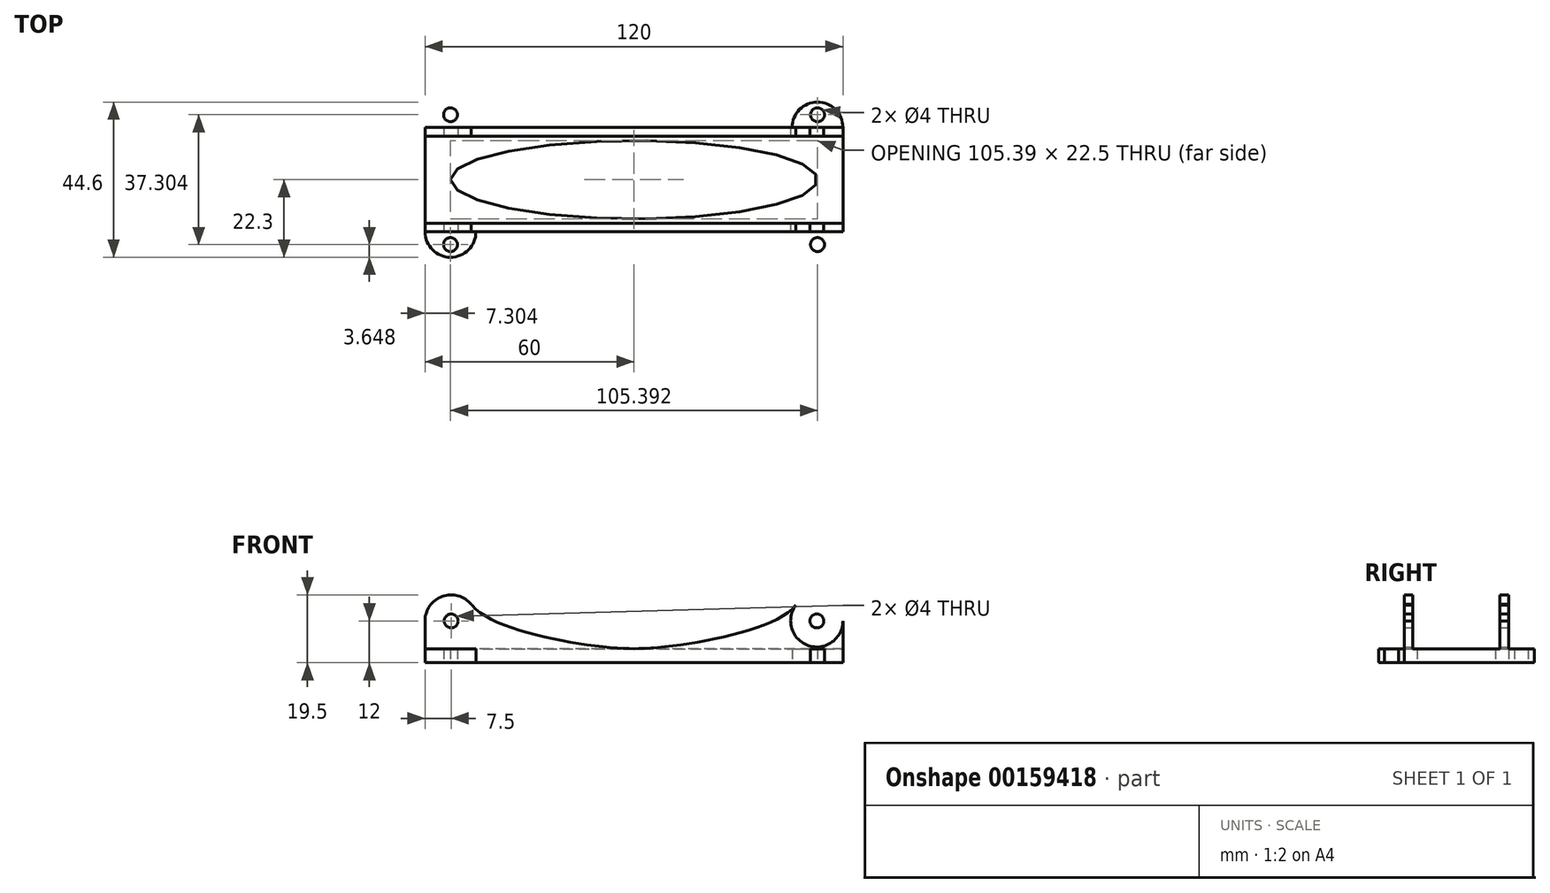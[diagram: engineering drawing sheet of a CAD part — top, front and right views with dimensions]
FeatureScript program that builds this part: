
annotation { "Feature Type Name" : "Feature", "Feature Type Description" : "" }
export const myFeature = defineFeature(function(context is Context, id is Id, definition is map)
    precondition{}
    {
        {
            assignVariable(context, id + "F0", {"mode" : VariableMode.ASSIGNED, "variableType" : VariableType.LENGTH, "measurementMode" : VariableMeasurementMode.DISTANCE, "name" : "channelWidth", "lengthValue" : 25 * mm, "minmax" : VariableMinMaxSelection.MINIMUM, "extendEntities" : false, "measureFromAxis" : false, "distance" : 0 * mm, "xOffset" : 0 * mm, "yOffset" : 0 * mm, "zOffset" : 0 * mm, "componentSelector" : AxisWithCustom.DISTANCE, "customOffset" : 0 * mm, "radius" : false, "description" : ""});
        }
        {
            var Q0;
            Q0=qCreatedBy(makeId("Front.planeOp"),FACE);
            var sketch = newSketch(context, id + "F1", { "sketchPlane" : qUnion([Q0])});
            skLineSegment(sketch, "E0", {"start": v(-52.5, 0) * mm, "end": v(52.5, 0) * mm, "construction": true});
            skPoint(sketch, "E1", {"position": v(-52.5, 0) * mm});
            skPoint(sketch, "E2", {"position": v(52.5, 0) * mm});
            skCircle(sketch, "E3", {"center": v(-52.5, 0) * mm, "radius": 7.5 * mm});
            skLineSegment(sketch, "E4", {"start": v(-60, 0) * mm, "end": v(-60, -12) * mm});
            skLineSegment(sketch, "E5", {"start": v(-60, -12) * mm, "end": v(0, -12) * mm});
            skLineSegment(sketch, "E6", {"start": v(0, -12) * mm, "end": v(0, -8) * mm});
            skFitSpline(sketch, "E7", {"points": [v(0, -8) * mm, v(-46.7, 4.76) * mm], "startDerivative": vector(-30.75, 0) * mm, "endDerivative": vector(-19.19, 25.66) * mm});
            skCircle(sketch, "E8", {"center": v(-52.5, 0) * mm, "radius": 2 * mm});
            skFitSpline(sketch, "E9.MirrorCS", {"points": [v(0, -8) * mm, v(46.7, 4.76) * mm], "startDerivative": vector(30.75, 0) * mm, "endDerivative": vector(19.19, 25.66) * mm});
            skLineSegment(sketch, "E10.MirrorCS", {"start": v(60, -12) * mm, "end": v(0, -12) * mm});
            skLineSegment(sketch, "E11.MirrorCS", {"start": v(60, 0) * mm, "end": v(60, -12) * mm});
            skCircle(sketch, "E12.MirrorC", {"center": v(52.5, 0) * mm, "radius": 7.5 * mm});
            skCircle(sketch, "E13.MirrorC", {"center": v(52.5, 0) * mm, "radius": 2 * mm});
            skLineSegment(sketch, "E14.bottom", {"start": v(0, -8) * mm, "end": v(-60, -8) * mm});
            skLineSegment(sketch, "E14.top", {"start": v(0, 11.94) * mm, "end": v(-60, 11.94) * mm});
            skLineSegment(sketch, "E14.left", {"start": v(0, -8) * mm, "end": v(0, 11.94) * mm});
            skLineSegment(sketch, "E14.right", {"start": v(-60, -8) * mm, "end": v(-60, 11.94) * mm});
            skLineSegment(sketch, "E15.MirrorCS", {"start": v(0, 11.94) * mm, "end": v(60, 11.94) * mm});
            skLineSegment(sketch, "E16.MirrorCS", {"start": v(60, -8) * mm, "end": v(60, 11.94) * mm});
            skLineSegment(sketch, "E17.MirrorCS", {"start": v(0, -8) * mm, "end": v(60, -8) * mm});
            skSolve(sketch);
        }
        {
            var Q0;
            {var subQ4=sQuery(id+"F1.wireOp",EDGE,"E4");Q0=makeQuery(id+"F1.imprint","IMPRINT",FACE,{"disambiguationData":[TD([[makeQuery(id+"F1.imprint","IMPRINT",EDGE,{"derivedFrom":subQ4}),1.0]])]});}
            var Q1;
            Q1=makeQuery(id+"F1.imprint","IMPRINT",FACE,{"disambiguationData":[TD([[makeQuery(id+"F1.imprint","IMPRINT",EDGE,{"derivedFrom":sQuery(id+"F1.wireOp",EDGE,"E8")}),-1.0]])]});
            var Q2;
            {var subQ1=sQuery(id+"F1.wireOp",EDGE,"E6");Q2=makeQuery(id+"F1.imprint","IMPRINT",FACE,{"disambiguationData":[TD([[makeQuery(id+"F1.imprint","IMPRINT",EDGE,{"derivedFrom":subQ1}),-1.0]])]});}
            var Q3;
            Q3=makeQuery(id+"F1.imprint","IMPRINT",FACE,{"disambiguationData":[TD([[makeQuery(id+"F1.imprint","IMPRINT",EDGE,{"derivedFrom":sQuery(id+"F1.wireOp",EDGE,"E13.MirrorC")}),1.0]])]});
            var Q4;
            {var subQ5=sQuery(id+"F1.wireOp",EDGE,"E14.bottom");Q4=makeQuery(id+"F1.imprint","IMPRINT",FACE,{"disambiguationData":[TD([[makeQuery(id+"F1.imprint","IMPRINT",EDGE,{"derivedFrom":subQ5}),-1.0]])]});}
            var Q5;
            {var subQ0=sQuery(id+"F1.wireOp",EDGE,"E17.MirrorCS");Q5=makeQuery(id+"F1.imprint","IMPRINT",FACE,{"disambiguationData":[TD([[makeQuery(id+"F1.imprint","IMPRINT",EDGE,{"derivedFrom":subQ0}),1.0]])]});}
            extrude(context, id + "F2", {"entities" : qUnion([Q0, Q1, Q2, Q3, Q4, Q5]), "flatOperationType" : FlatOperationType.REMOVE, "offsetDistance" : 25 * mm, "depth" : getVariable(context, 'channelWidth') + 5 * mm, "symmetric" : true, "domain" : OperationDomain.MODEL});
        }
        {
            var Q0;
            {var subQ4=sQuery(id+"F1.wireOp",EDGE,"E14.top");Q0=makeQuery(id+"F1.imprint","IMPRINT",FACE,{"disambiguationData":[TD([[makeQuery(id+"F1.imprint","IMPRINT",EDGE,{"derivedFrom":subQ4}),1.0]])]});}
            var Q1;
            {var subQ0=sQuery(id+"F1.wireOp",EDGE,"E14.left");Q1=makeQuery(id+"F1.imprint","IMPRINT",FACE,{"disambiguationData":[TD([[makeQuery(id+"F1.imprint","IMPRINT",EDGE,{"derivedFrom":subQ0}),-1.0]])]});}
            var Q2;
            Q2=makeQuery(id+"F1.imprint","IMPRINT",FACE,{"disambiguationData":[TD([[makeQuery(id+"F1.imprint","IMPRINT",EDGE,{"derivedFrom":sQuery(id+"F1.wireOp",EDGE,"E8")}),-1.0]])]});
            var Q3;
            Q3=makeQuery(id+"F1.imprint","IMPRINT",FACE,{"disambiguationData":[TD([[makeQuery(id+"F1.imprint","IMPRINT",EDGE,{"derivedFrom":sQuery(id+"F1.wireOp",EDGE,"E8")}),1.0]])]});
            var Q4;
            {var subQ5=sQuery(id+"F1.wireOp",EDGE,"E14.bottom");Q4=makeQuery(id+"F1.imprint","IMPRINT",FACE,{"disambiguationData":[TD([[makeQuery(id+"F1.imprint","IMPRINT",EDGE,{"derivedFrom":subQ5}),-1.0]])]});}
            var Q5;
            {var subQ0=sQuery(id+"F1.wireOp",EDGE,"E17.MirrorCS");Q5=makeQuery(id+"F1.imprint","IMPRINT",FACE,{"disambiguationData":[TD([[makeQuery(id+"F1.imprint","IMPRINT",EDGE,{"derivedFrom":subQ0}),1.0]])]});}
            var Q6;
            Q6=makeQuery(id+"F1.imprint","IMPRINT",FACE,{"disambiguationData":[TD([[makeQuery(id+"F1.imprint","IMPRINT",EDGE,{"derivedFrom":sQuery(id+"F1.wireOp",EDGE,"E13.MirrorC")}),1.0]])]});
            var Q7;
            Q7=makeQuery(id+"F1.imprint","IMPRINT",FACE,{"disambiguationData":[TD([[makeQuery(id+"F1.imprint","IMPRINT",EDGE,{"derivedFrom":sQuery(id+"F1.wireOp",EDGE,"E13.MirrorC")}),-1.0]])]});
            extrude(context, id + "F3", {"entities" : qUnion([Q0, Q1, Q2, Q3, Q4, Q5, Q6, Q7]), "operationType" : NewBodyOperationType.REMOVE, "flatOperationType" : FlatOperationType.REMOVE, "oppositeDirection" : true, "offsetDistance" : 25 * mm, "depth" : getVariable(context, 'channelWidth'), "symmetric" : true, "domain" : OperationDomain.MODEL});
        }
        {
            var Q0;
            Q0=makeQuery(id+"F2.opExtrude","SWEPT_FACE",FACE,{"disambiguationData":[OSD([sQuery(id+"F1.wireOp",EDGE,"E5"),sQuery(id+"F1.wireOp",EDGE,"E10.MirrorCS")])]});
            var sketch = newSketch(context, id + "F4", { "sketchPlane" : qUnion([Q0])});
            skLineSegment(sketch, "E18", {"start": v(-52.7, 0) * mm, "end": v(-52.7, 15) * mm, "construction": true});
            skCircle(sketch, "E19", {"center": v(-52.7, 15) * mm, "radius": 7.3 * mm});
            skLineSegment(sketch, "E20", {"start": v(-52.7, 15) * mm, "end": v(-52.7, 22.3) * mm, "construction": true});
            skPoint(sketch, "E21", {"position": v(-52.7, 18.65) * mm});
            skCircle(sketch, "E22", {"center": v(-52.7, 18.65) * mm, "radius": 2 * mm});
            skCircle(sketch, "E23.MirrorC", {"center": v(-52.7, -18.65) * mm, "radius": 2 * mm});
            skCircle(sketch, "E24.MirrorC", {"center": v(-52.7, -15) * mm, "radius": 7.3 * mm});
            skCircle(sketch, "E25.MirrorC", {"center": v(52.7, 15) * mm, "radius": 7.3 * mm});
            skCircle(sketch, "E26.MirrorC", {"center": v(52.7, 18.65) * mm, "radius": 2 * mm});
            skCircle(sketch, "E27.MirrorC", {"center": v(52.7, -15) * mm, "radius": 7.3 * mm});
            skCircle(sketch, "E28.MirrorC", {"center": v(52.7, -18.65) * mm, "radius": 2 * mm});
            skEllipse(sketch, "E29", {"center": v(0, 0) * mm, "majorRadius": 52.7 * mm, "minorRadius": 11.25 * mm, "majorAxis": v(-1, 0)});
            skSolve(sketch);
        }
        {
            var Q0;
            Q0=makeQuery(id+"F4.imprint","IMPRINT",FACE,{"disambiguationData":[TD([[makeQuery(id+"F4.imprint","IMPRINT",EDGE,{"derivedFrom":sQuery(id+"F4.wireOp",EDGE,"E22")}),-1.0]])]});
            var Q1;
            Q1=makeQuery(id+"F4.imprint","IMPRINT",FACE,{"disambiguationData":[TD([[makeQuery(id+"F4.imprint","IMPRINT",EDGE,{"derivedFrom":sQuery(id+"F4.wireOp",EDGE,"E23.MirrorC")}),1.0]])]});
            var Q2;
            Q2=makeQuery(id+"F4.imprint","IMPRINT",FACE,{"disambiguationData":[TD([[makeQuery(id+"F4.imprint","IMPRINT",EDGE,{"derivedFrom":sQuery(id+"F4.wireOp",EDGE,"E26.MirrorC")}),1.0]])]});
            var Q3;
            Q3=makeQuery(id+"F4.imprint","IMPRINT",FACE,{"disambiguationData":[TD([[makeQuery(id+"F4.imprint","IMPRINT",EDGE,{"derivedFrom":sQuery(id+"F4.wireOp",EDGE,"E28.MirrorC")}),-1.0]])]});
            extrude(context, id + "F5", {"entities" : qUnion([Q0, Q1, Q2, Q3]), "operationType" : NewBodyOperationType.ADD, "oppositeDirection" : true, "depth" : 4 * mm});
        }
        {
            var Q0;
            Q0=makeQuery(id+"F4.imprint","IMPRINT",FACE,{"disambiguationData":[TD([[makeQuery(id+"F4.imprint","IMPRINT",EDGE,{"derivedFrom":sQuery(id+"F4.wireOp",EDGE,"E29")}),1.0]])]});
            extrude(context, id + "F6", {"entities" : qUnion([Q0]), "operationType" : NewBodyOperationType.REMOVE, "oppositeDirection" : true, "depth" : 25 * mm});
        }
    });
